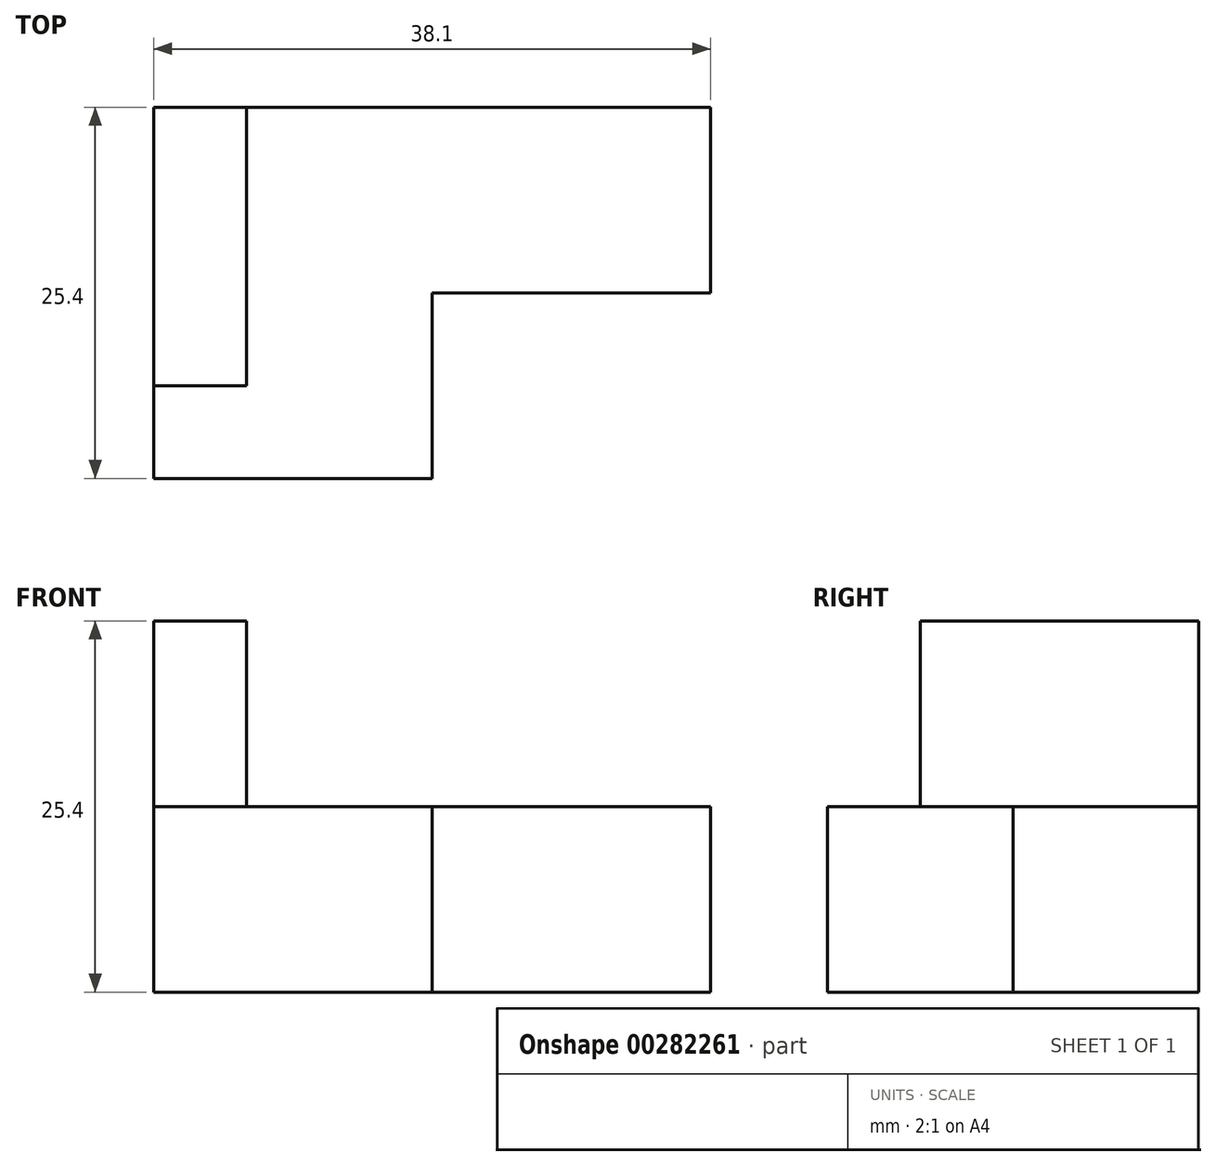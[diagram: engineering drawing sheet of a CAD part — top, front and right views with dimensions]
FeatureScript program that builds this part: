
annotation { "Feature Type Name" : "Feature", "Feature Type Description" : "" }
export const myFeature = defineFeature(function(context is Context, id is Id, definition is map)
    precondition{}
    {
        {
            var Q0;
            Q0=qCreatedBy(makeId("Top.planeOp"),FACE);
            var sketch = newSketch(context, id + "F0", { "sketchPlane" : qUnion([Q0])});
            skLineSegment(sketch, "E0.bottom", {"start": v(0, 0) * mm, "end": v(38.1, 0) * mm});
            skLineSegment(sketch, "E0.top", {"start": v(0, -25.4) * mm, "end": v(38.1, -25.4) * mm});
            skLineSegment(sketch, "E0.left", {"start": v(0, 0) * mm, "end": v(0, -25.4) * mm});
            skLineSegment(sketch, "E0.right", {"start": v(38.1, 0) * mm, "end": v(38.1, -25.4) * mm});
            skSolve(sketch);
        }
        {
            var Q0;
            Q0 = qSketchRegion(id + "F0", true);
            extrude(context, id + "F1", {"entities" : qUnion([Q0]), "depth" : 12.7 * mm});
        }
        {
            var Q0;
            Q0=makeQuery(id+"F1.opExtrude","CAP_FACE",FACE,{"disambiguationData":[OSD([sQuery(id+"F0.wireOp",EDGE,"E0.bottom"),sQuery(id+"F0.wireOp",EDGE,"E0.top"),sQuery(id+"F0.wireOp",EDGE,"E0.left"),sQuery(id+"F0.wireOp",EDGE,"E0.right")])],"isStart":false});
            var sketch = newSketch(context, id + "F2", { "sketchPlane" : qUnion([Q0])});
            skLineSegment(sketch, "E1.bottom", {"start": v(38.1, -25.4) * mm, "end": v(19.05, -25.4) * mm});
            skLineSegment(sketch, "E1.top", {"start": v(38.1, -12.7) * mm, "end": v(19.05, -12.7) * mm});
            skLineSegment(sketch, "E1.left", {"start": v(38.1, -25.4) * mm, "end": v(38.1, -12.7) * mm});
            skLineSegment(sketch, "E1.right", {"start": v(19.05, -25.4) * mm, "end": v(19.05, -12.7) * mm});
            skSolve(sketch);
        }
        {
            var Q0;
            Q0 = qSketchRegion(id + "F2", true);
            extrude(context, id + "F3", {"entities" : qUnion([Q0]), "operationType" : NewBodyOperationType.REMOVE, "endBound" : BoundingType.THROUGH_ALL, "oppositeDirection" : true, "depth" : 25.4 * mm});
        }
        {
            var Q0;
            Q0=makeQuery(id+"F1.opExtrude","CAP_FACE",FACE,{"disambiguationData":[OSD([sQuery(id+"F0.wireOp",EDGE,"E0.bottom"),sQuery(id+"F0.wireOp",EDGE,"E0.top"),sQuery(id+"F0.wireOp",EDGE,"E0.left"),sQuery(id+"F0.wireOp",EDGE,"E0.right")])],"isStart":false});
            var sketch = newSketch(context, id + "F4", { "sketchPlane" : qUnion([Q0])});
            skLineSegment(sketch, "E2.bottom", {"start": v(0, 0) * mm, "end": v(6.35, 0) * mm});
            skLineSegment(sketch, "E2.top", {"start": v(0, -19.05) * mm, "end": v(6.35, -19.05) * mm});
            skLineSegment(sketch, "E2.left", {"start": v(0, 0) * mm, "end": v(0, -19.05) * mm});
            skLineSegment(sketch, "E2.right", {"start": v(6.35, 0) * mm, "end": v(6.35, -19.05) * mm});
            skSolve(sketch);
        }
        {
            var Q0;
            Q0 = qSketchRegion(id + "F4", true);
            extrude(context, id + "F5", {"entities" : qUnion([Q0]), "operationType" : NewBodyOperationType.ADD, "depth" : 12.7 * mm});
        }
    });
